# Revit family: Stream_Eng
name_source: partatom
category: Mechanical Equipment
units: mm (PartAtom-declared; Revit-internal decimal feet)

## family parameters
Always vertical = Yes
Classification = None
Cut with Voids When Loaded = No
Part Type = Normal
Room Calculation Point = No
Round Connector Dimension = Use Diameter
Shared = No
Work Plane-Based = No

## types (4) — shared parameters
00_20_Manufacturer = Vents
00_20_Name = Sound-insulated fan
Amperage = 0 A
B = 253 mm  [stored 0.830052 ft]
Frequency = 50 Hz
H = 273 mm  [stored 0.895669 ft]
Height = 273 mm  [stored 0.895669 ft]
Load Classification = HVAC
Maintenance zone material = <By Category>
Manufacturer = Vents
Number of Fase = 1
URL = https://ventilation-system.com
Voltage = 230 V
Weight = 5.00 kg
Width = 253 mm  [stored 0.830052 ft]
r3 = 120 mm  [stored 0.393701 ft]
zero-valued in all types: Default Elevation

## per-type parameters (varying)
| type | Casing Material | D | D1 | Diameter | Frame | L | L1 | Length | Maximum Air Flow | Power | l1 | l2 | l3 | l4 | l5 | l6 | r | r1 | r2 | r22 |
| Stream 100/125 (spigot 100 mm) | Пластмаса, непрозора, біла | 100 mm  [stored 0.328084 ft] | 98 mm  [stored 0.321522 ft] | 100 mm  [stored 0.328084 ft] | Frame : 100 | 752 mm | 577 mm | 752 mm | 61.0 L/s | 32 W | 30 mm | 42 mm | 68 mm | 83 mm | 125 mm  [stored 0.410105 ft] | 180 mm | 50 mm  [stored 0.164042 ft] | 60 mm  [stored 0.19685 ft] | 66 mm  [stored 0.216535 ft] | 68 mm |
| Stream 100/125 (spigot 125 mm) | Metal, painted, blue, matte RAL 5007 | 125 mm  [stored 0.410105 ft] | 123 mm  [stored 0.403543 ft] | 125 mm  [stored 0.410105 ft] | Frame : 125 | 679 mm | 520 mm | 679 mm | 89.0 L/s | 34 W | 27 mm | 38 mm | 61 mm | 75 mm | 113 mm | 163 mm | 63 mm | 75 mm | 83 mm | 85 mm |
| Stream 150/160 (spigot 150 mm) | Metal, painted, blue, matte RAL 5007 | 150 mm | 148 mm  [stored 0.485564 ft] | 150 mm | Frame : 150 | 606 mm | 463 mm | 606 mm | 150.0 L/s | 51 W | 24 mm | 34 mm | 55 mm | 67 mm | 101 mm | 145 mm  [stored 0.475722 ft] | 75 mm | 90 mm  [stored 0.295276 ft] | 99 mm  [stored 0.324803 ft] | 101 mm |
| Stream 150/160 (spigot 160 mm) | Metal, painted, blue, matte RAL 5007 | 160 mm  [stored 0.524934 ft] | 158 mm | 160 mm  [stored 0.524934 ft] | Frame : 160 | 606 mm | 463 mm | 606 mm | 150.0 L/s | 51 W | 24 mm | 34 mm | 55 mm | 67 mm | 101 mm | 145 mm  [stored 0.475722 ft] | 80 mm  [stored 0.262467 ft] | 96 mm  [stored 0.314961 ft] | 106 mm | 108 mm |

note: column(s) folded — value = type name in every type: 00_20_Type

note: [stored X ft] marks values corroborated as IEEE doubles in the binary element streams (Revit-internal decimal feet)
